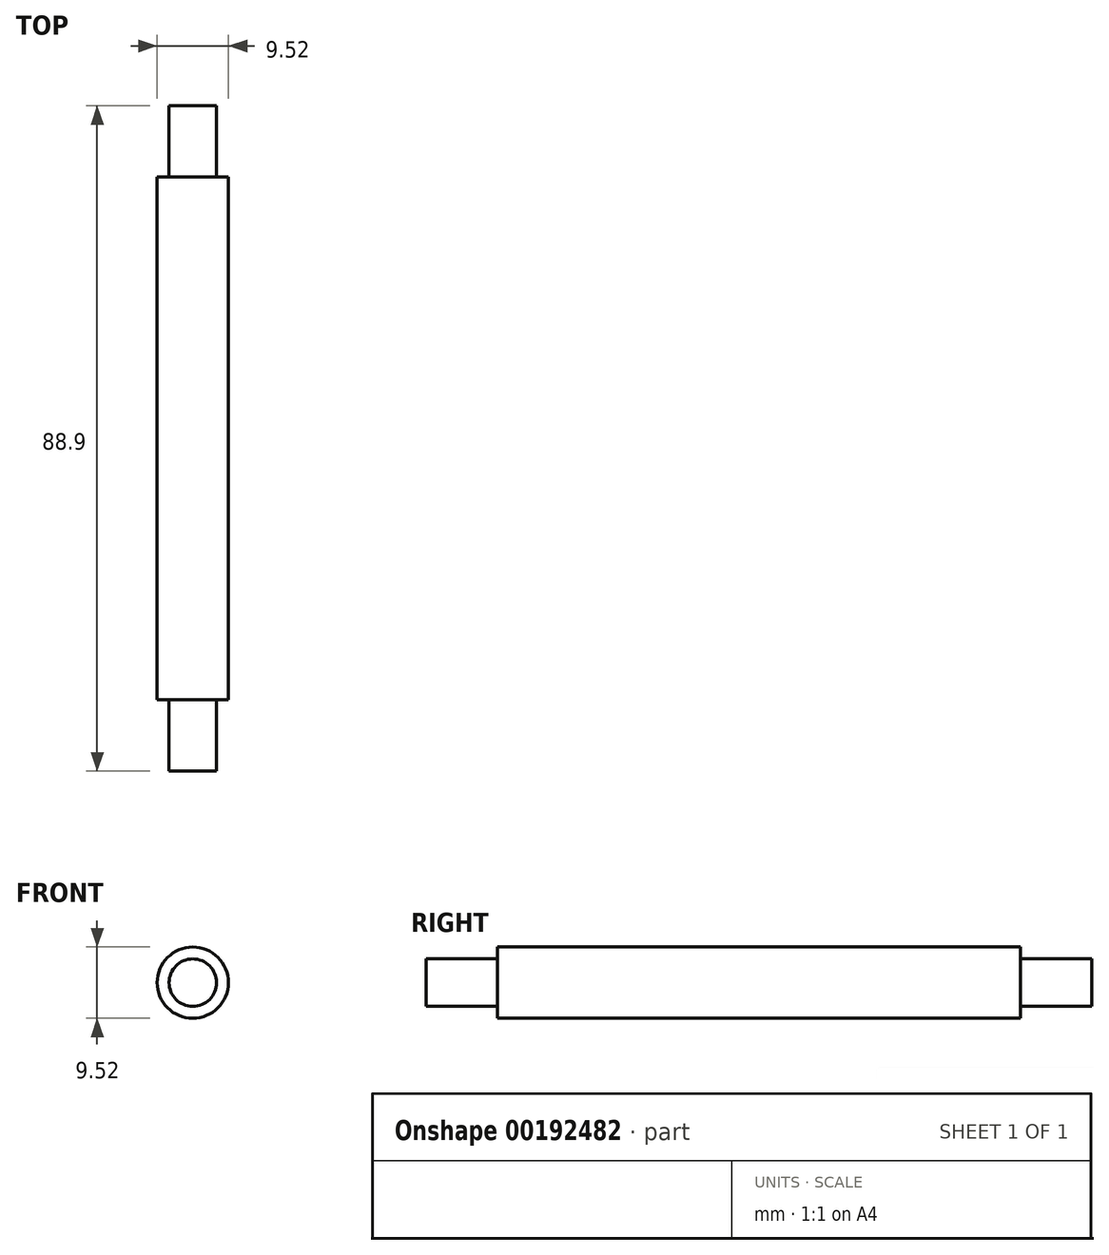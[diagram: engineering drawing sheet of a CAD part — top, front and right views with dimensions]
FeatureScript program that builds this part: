
annotation { "Feature Type Name" : "Feature", "Feature Type Description" : "" }
export const myFeature = defineFeature(function(context is Context, id is Id, definition is map)
    precondition{}
    {
        {
            var Q0;
            Q0=qCreatedBy(makeId("Front.planeOp"),FACE);
            var sketch = newSketch(context, id + "F0", { "sketchPlane" : qUnion([Q0])});
            skCircle(sketch, "E0", {"center": v(0, 0) * mm, "radius": 4.76 * mm});
            skSolve(sketch);
        }
        {
            var Q0;
            Q0 = qSketchRegion(id + "F0", true);
            extrude(context, id + "F1", {"entities" : qUnion([Q0]), "endBound" : BoundingType.SYMMETRIC, "depth" : 88.9 * mm});
        }
        {
            var Q0;
            Q0=makeQuery(id+"F1.opExtrude","CAP_FACE",FACE,{"disambiguationData":[OSD([sQuery(id+"F0.wireOp",EDGE,"E0")])],"isStart":false});
            var sketch = newSketch(context, id + "F2", { "sketchPlane" : qUnion([Q0])});
            skCircle(sketch, "E1", {"center": v(0, 0) * mm, "radius": 3.18 * mm});
            skCircle(sketch, "E2", {"center": v(0, 0) * mm, "radius": 6.35 * mm});
            skSolve(sketch);
        }
        {
            var Q0;
            Q0 = qSketchRegion(id + "F2", true);
            extrude(context, id + "F3", {"entities" : qUnion([Q0]), "operationType" : NewBodyOperationType.REMOVE, "oppositeDirection" : true, "depth" : 9.52 * mm});
        }
        {
            var Q0;
            Q0=makeQuery(id+"F1.opExtrude","CAP_FACE",FACE,{"disambiguationData":[OSD([sQuery(id+"F0.wireOp",EDGE,"E0")])],"isStart":true});
            var sketch = newSketch(context, id + "F4", { "sketchPlane" : qUnion([Q0])});
            skCircle(sketch, "E3", {"center": v(0, 0) * mm, "radius": 3.18 * mm});
            skCircle(sketch, "E4", {"center": v(0, 0) * mm, "radius": 6.35 * mm});
            skSolve(sketch);
        }
        {
            var Q0;
            Q0 = qSketchRegion(id + "F4", true);
            extrude(context, id + "F5", {"entities" : qUnion([Q0]), "operationType" : NewBodyOperationType.REMOVE, "oppositeDirection" : true, "depth" : 9.52 * mm});
        }
    });
